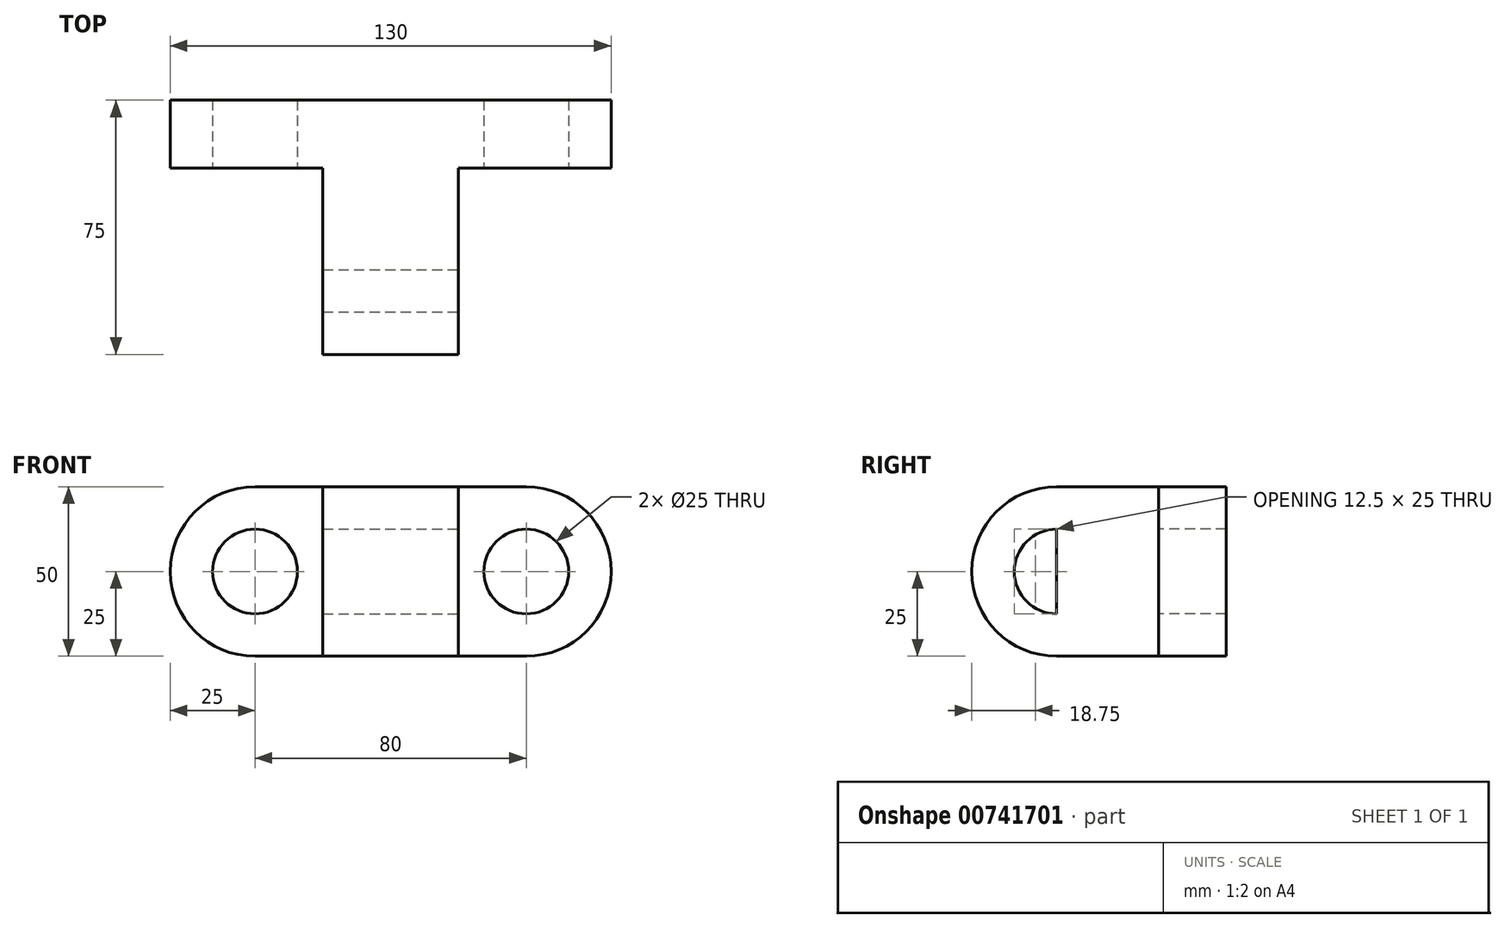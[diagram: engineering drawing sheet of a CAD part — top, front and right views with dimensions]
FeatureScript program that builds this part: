
annotation { "Feature Type Name" : "Feature", "Feature Type Description" : "" }
export const myFeature = defineFeature(function(context is Context, id is Id, definition is map)
    precondition{}
    {
        {
            var Q0;
            Q0=qCreatedBy(makeId("Front.planeOp"),FACE);
            var sketch = newSketch(context, id + "F0", { "sketchPlane" : qUnion([Q0])});
            skLineSegment(sketch, "E0", {"start": v(0, 0) * mm, "end": v(0, 50) * mm});
            skLineSegment(sketch, "E1", {"start": v(0, 50) * mm, "end": v(80, 50) * mm});
            skLineSegment(sketch, "E2", {"start": v(80, 50) * mm, "end": v(80, 0) * mm});
            skLineSegment(sketch, "E3", {"start": v(80, 0) * mm, "end": v(0, 0) * mm});
            skArc(sketch, "E4", {"start": v(0, 50) * mm, "mid": v(-25, 25) * mm, "end": v(0, 0) * mm});
            skArc(sketch, "E5", {"start": v(80, 0) * mm, "mid": v(105, 25) * mm, "end": v(80, 50) * mm});
            skLineSegment(sketch, "E6", {"start": v(20, 0) * mm, "end": v(20, 50) * mm});
            skLineSegment(sketch, "E7", {"start": v(60, 50) * mm, "end": v(60, 0) * mm});
            skCircle(sketch, "E8", {"center": v(0, 25) * mm, "radius": 12.5 * mm});
            skCircle(sketch, "E9", {"center": v(80, 25) * mm, "radius": 12.5 * mm});
            skSolve(sketch);
        }
        {
            var Q0;
            Q0 = qSketchRegion(id + "F0", true);
            extrude(context, id + "F1", {"entities" : qUnion([Q0]), "depth" : -20 * mm, "offsetDistance" : 25 * mm});
        }
        {
            var Q0;
            {var subQ0=sQuery(id+"F0.wireOp",EDGE,"E6");Q0=makeQuery(id+"F0.imprint","IMPRINT",FACE,{"disambiguationData":[TD([[makeQuery(id+"F0.imprint","IMPRINT",EDGE,{"derivedFrom":subQ0}),-1.0]])]});}
            extrude(context, id + "F2", {"entities" : qUnion([Q0]), "operationType" : NewBodyOperationType.ADD, "depth" : 30 * mm, "offsetDistance" : 25 * mm});
        }
        {
            var Q0;
            Q0=makeQuery(id+"F2.opExtrude","SWEPT_FACE",FACE,{"disambiguationData":[OSD([sQuery(id+"F0.wireOp",EDGE,"E7")])]});
            var sketch = newSketch(context, id + "F3", { "sketchPlane" : qUnion([Q0])});
            skArc(sketch, "E10", {"start": v(-30, 50) * mm, "mid": v(-55, 25) * mm, "end": v(-30, 0) * mm});
            skCircle(sketch, "E11", {"center": v(-30, 25) * mm, "radius": 12.5 * mm});
            skSolve(sketch);
        }
        {
            var Q0;
            Q0=makeQuery(id+"F3.imprint","IMPRINT",FACE,{"disambiguationData":[TD([[makeQuery(id+"F3.imprint","IMPRINT",EDGE,{"derivedFrom":sQuery(id+"F3.wireOp",EDGE,"E10")}),1.0]])]});
            extrude(context, id + "F4", {"entities" : qUnion([Q0]), "operationType" : NewBodyOperationType.ADD, "depth" : -40 * mm, "offsetDistance" : 25 * mm});
        }
        {
            var Q0;
            {var subQ0=sQuery(id+"F3.wireOp",EDGE,"E11");var subQ1=makeQuery(id+"F2.opExtrude","CAP_EDGE",EDGE,{"disambiguationData":[OSD([sQuery(id+"F0.wireOp",EDGE,"E7")])],"isStart":false});var subQ2=makeQuery(id+"F3.imprint","INTERSECT",VERTEX,{"disambiguationData":[OD(0.0)],"derivedFrom":[subQ1,subQ0]});Q0=makeQuery(id+"F3.imprint","IMPRINT",FACE,{"disambiguationData":[TD([[makeQuery(id+"F3.imprint","IMPRINT",EDGE,{"disambiguationData":[TD([[subQ2,1.0]])],"derivedFrom":subQ0}),1.0]])]});}
            extrude(context, id + "F5", {"entities" : qUnion([Q0]), "operationType" : NewBodyOperationType.REMOVE, "oppositeDirection" : true, "depth" : 40 * mm, "offsetDistance" : 25 * mm});
        }
    });
